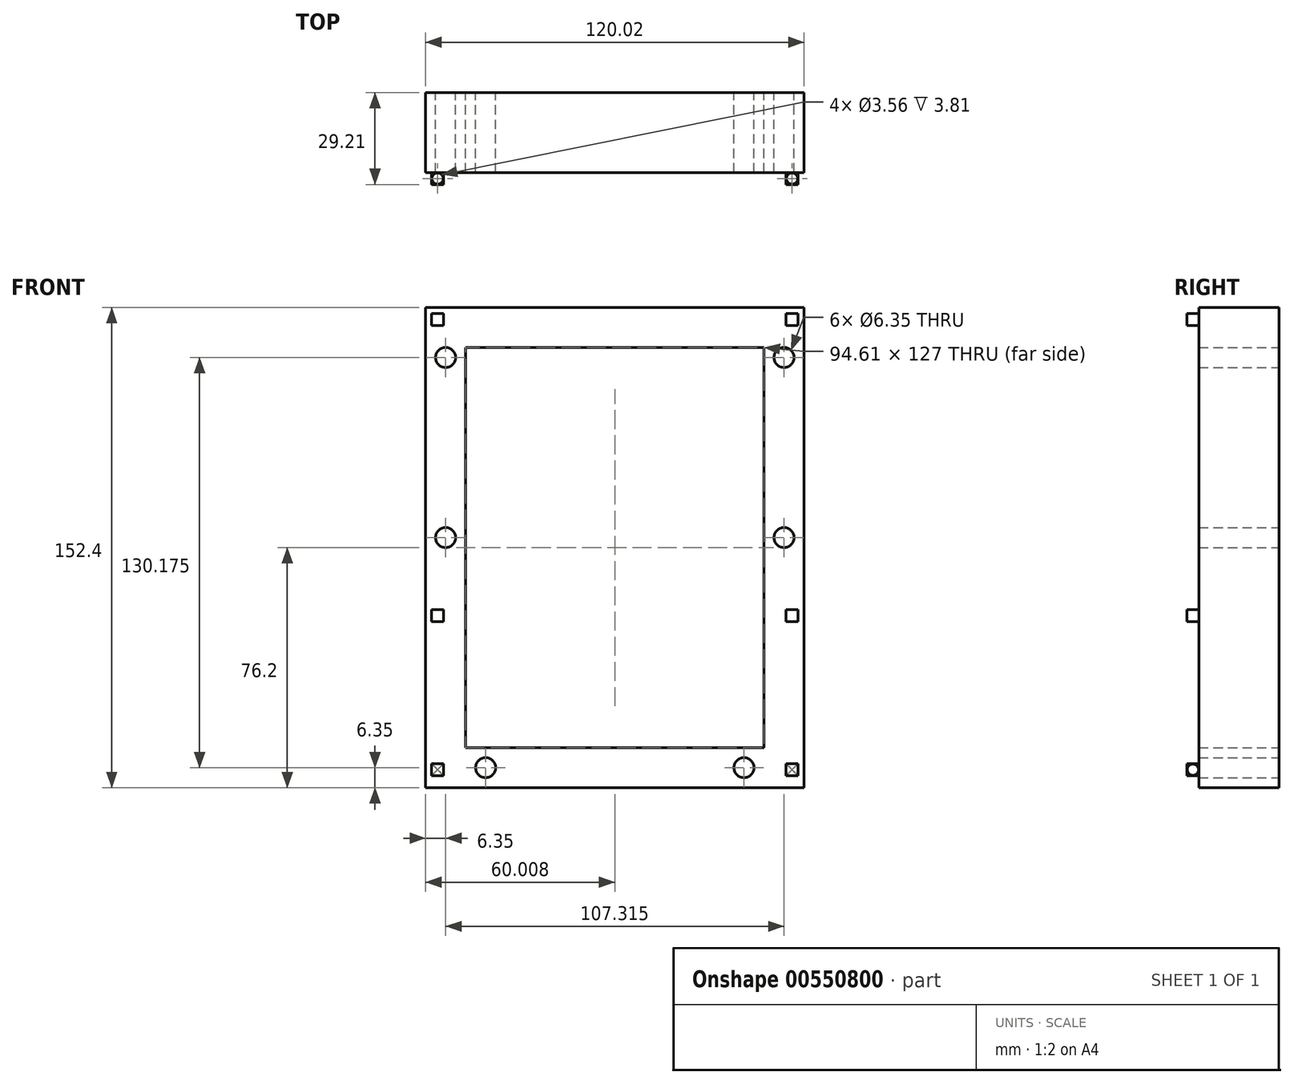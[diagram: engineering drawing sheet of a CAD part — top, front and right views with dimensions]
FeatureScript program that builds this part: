
annotation { "Feature Type Name" : "Feature", "Feature Type Description" : "" }
export const myFeature = defineFeature(function(context is Context, id is Id, definition is map)
    precondition{}
    {
        {
            var Q0;
            Q0=qCreatedBy(makeId("Front.planeOp"),FACE);
            var sketch = newSketch(context, id + "F0", { "sketchPlane" : qUnion([Q0])});
            skLineSegment(sketch, "E0.bottom", {"start": v(0, 0) * mm, "end": v(120.02, 0) * mm});
            skLineSegment(sketch, "E0.top", {"start": v(0, -152.4) * mm, "end": v(120.02, -152.4) * mm});
            skLineSegment(sketch, "E0.left", {"start": v(0, 0) * mm, "end": v(0, -152.4) * mm});
            skLineSegment(sketch, "E0.right", {"start": v(120.02, 0) * mm, "end": v(120.02, -152.4) * mm});
            skLineSegment(sketch, "E1", {"start": v(12.7, -12.7) * mm, "end": v(12.7, -139.7) * mm});
            skLineSegment(sketch, "E2", {"start": v(12.7, -12.7) * mm, "end": v(107.31, -12.7) * mm});
            skLineSegment(sketch, "E3", {"start": v(107.31, -12.7) * mm, "end": v(107.31, -139.7) * mm});
            skLineSegment(sketch, "E4", {"start": v(12.7, -139.7) * mm, "end": v(107.31, -139.7) * mm});
            skCircle(sketch, "E5", {"center": v(6.35, -15.88) * mm, "radius": 3.18 * mm});
            skCircle(sketch, "E6", {"center": v(6.35, -73.03) * mm, "radius": 3.18 * mm});
            skCircle(sketch, "E7", {"center": v(19.05, -146.05) * mm, "radius": 3.18 * mm});
            skLineSegment(sketch, "E8", {"start": v(60, 0) * mm, "end": v(60, -152.4) * mm, "construction": true});
            skCircle(sketch, "E9.MirrorC", {"center": v(113.66, -15.87) * mm, "radius": 3.18 * mm});
            skCircle(sketch, "E10.MirrorC", {"center": v(113.67, -73.03) * mm, "radius": 3.18 * mm});
            skCircle(sketch, "E11.MirrorC", {"center": v(100.97, -146.05) * mm, "radius": 3.18 * mm});
            skLineSegment(sketch, "E12", {"start": v(120.02, -101.6) * mm, "end": v(0, -101.6) * mm, "construction": true});
            skLineSegment(sketch, "E13", {"start": v(0, -7.62) * mm, "end": v(120.01, -7.62) * mm, "construction": true});
            skLineSegment(sketch, "E14", {"start": v(0, -93.98) * mm, "end": v(120.01, -93.98) * mm, "construction": true});
            skLineSegment(sketch, "E15", {"start": v(7.62, -101.6) * mm, "end": v(7.62, -152.4) * mm, "construction": true});
            skLineSegment(sketch, "E16", {"start": v(112.4, -101.6) * mm, "end": v(112.4, -152.4) * mm, "construction": true});
            skLineSegment(sketch, "E17.bottom", {"start": v(1.9, -144.78) * mm, "end": v(5.72, -144.78) * mm});
            skLineSegment(sketch, "E17.top", {"start": v(1.9, -148.6) * mm, "end": v(5.72, -148.6) * mm});
            skLineSegment(sketch, "E17.left", {"start": v(1.9, -144.78) * mm, "end": v(1.9, -148.59) * mm});
            skLineSegment(sketch, "E17.right", {"start": v(5.72, -144.78) * mm, "end": v(5.72, -148.59) * mm});
            skLineSegment(sketch, "E18.MirrorCS", {"start": v(118.11, -148.6) * mm, "end": v(114.3, -148.6) * mm});
            skLineSegment(sketch, "E19.MirrorCS", {"start": v(118.11, -144.78) * mm, "end": v(118.11, -148.59) * mm});
            skLineSegment(sketch, "E20.MirrorCS", {"start": v(118.11, -144.78) * mm, "end": v(114.3, -144.78) * mm});
            skLineSegment(sketch, "E21.MirrorCS", {"start": v(114.3, -144.78) * mm, "end": v(114.3, -148.59) * mm});
            skLineSegment(sketch, "E22.top", {"start": v(1.9, -101.6) * mm, "end": v(7.62, -101.6) * mm});
            skLineSegment(sketch, "E23", {"start": v(7.62, -101.6) * mm, "end": v(7.62, 0) * mm, "construction": true});
            skLineSegment(sketch, "E24.bottom", {"start": v(1.9, -95.88) * mm, "end": v(5.72, -95.88) * mm});
            skLineSegment(sketch, "E24.top", {"start": v(1.9, -99.7) * mm, "end": v(5.72, -99.7) * mm});
            skLineSegment(sketch, "E24.left", {"start": v(1.9, -95.88) * mm, "end": v(1.9, -99.7) * mm});
            skLineSegment(sketch, "E24.right", {"start": v(5.72, -95.88) * mm, "end": v(5.72, -99.7) * mm});
            skLineSegment(sketch, "E25.MirrorCS", {"start": v(118.11, -99.7) * mm, "end": v(114.3, -99.7) * mm});
            skLineSegment(sketch, "E26.MirrorCS", {"start": v(118.11, -95.88) * mm, "end": v(118.11, -99.7) * mm});
            skLineSegment(sketch, "E27.MirrorCS", {"start": v(118.11, -95.88) * mm, "end": v(114.3, -95.88) * mm});
            skLineSegment(sketch, "E28.MirrorCS", {"start": v(114.3, -95.88) * mm, "end": v(114.3, -99.7) * mm});
            skLineSegment(sketch, "E29.bottom", {"start": v(1.9, -1.9) * mm, "end": v(5.71, -1.9) * mm});
            skLineSegment(sketch, "E29.top", {"start": v(1.9, -5.71) * mm, "end": v(5.71, -5.71) * mm});
            skLineSegment(sketch, "E29.left", {"start": v(1.9, -1.9) * mm, "end": v(1.9, -5.71) * mm});
            skLineSegment(sketch, "E29.right", {"start": v(5.71, -1.9) * mm, "end": v(5.71, -5.71) * mm});
            skLineSegment(sketch, "E30.MirrorCS", {"start": v(118.11, -5.71) * mm, "end": v(114.3, -5.71) * mm});
            skLineSegment(sketch, "E31.MirrorCS", {"start": v(118.11, -1.9) * mm, "end": v(118.11, -5.71) * mm});
            skLineSegment(sketch, "E32.MirrorCS", {"start": v(118.11, -1.9) * mm, "end": v(114.3, -1.9) * mm});
            skLineSegment(sketch, "E33.MirrorCS", {"start": v(114.3, -1.9) * mm, "end": v(114.3, -5.72) * mm});
            skSolve(sketch);
        }
        {
            var Q0;
            Q0=makeQuery(id+"F0.imprint","IMPRINT",FACE,{"disambiguationData":[TD([[makeQuery(id+"F0.imprint","IMPRINT",EDGE,{"derivedFrom":sQuery(id+"F0.wireOp",EDGE,"E0.bottom")}),-1.0]])]});
            extrude(context, id + "F1", {"entities" : qUnion([Q0]), "depth" : 25.4 * mm, "offsetDistance" : 25.4 * mm});
        }
        {
            var Q0;
            Q0=makeQuery(id+"F0.imprint","IMPRINT",FACE,{"disambiguationData":[TD([[makeQuery(id+"F0.imprint","IMPRINT",EDGE,{"derivedFrom":sQuery(id+"F0.wireOp",EDGE,"E18.MirrorCS")}),-1.0]])]});
            var Q1;
            Q1=makeQuery(id+"F0.imprint","IMPRINT",FACE,{"disambiguationData":[TD([[makeQuery(id+"F0.imprint","IMPRINT",EDGE,{"derivedFrom":sQuery(id+"F0.wireOp",EDGE,"E17.bottom")}),-1.0]])]});
            extrude(context, id + "F2", {"entities" : qUnion([Q0, Q1]), "operationType" : NewBodyOperationType.ADD, "depth" : 29.2 * mm, "offsetDistance" : 25.4 * mm});
        }
        {
            var Q0;
            Q0=makeQuery(id+"F2.opExtrude","SWEPT_FACE",FACE,{"disambiguationData":[OSD([sQuery(id+"F0.wireOp",EDGE,"E17.left")])]});
            var sketch = newSketch(context, id + "F3", { "sketchPlane" : qUnion([Q0])});
            skCircle(sketch, "E34", {"center": v(27.3, -146.68) * mm, "radius": 1.78 * mm});
            skSolve(sketch);
        }
        {
            var Q0;
            Q0=makeQuery(id+"F3.imprint","IMPRINT",FACE,{"disambiguationData":[TD([[makeQuery(id+"F3.imprint","IMPRINT",EDGE,{"derivedFrom":sQuery(id+"F3.wireOp",EDGE,"E34")}),1.0]])]});
            extrude(context, id + "F4", {"entities" : qUnion([Q0]), "operationType" : NewBodyOperationType.REMOVE, "endBound" : BoundingType.THROUGH_ALL, "oppositeDirection" : true, "depth" : 25.4 * mm, "offsetDistance" : 25.4 * mm});
        }
        {
            var Q0;
            Q0=makeQuery(id+"F0.imprint","IMPRINT",FACE,{"disambiguationData":[TD([[makeQuery(id+"F0.imprint","IMPRINT",EDGE,{"derivedFrom":sQuery(id+"F0.wireOp",EDGE,"E25.MirrorCS")}),-1.0]])]});
            var Q1;
            Q1=makeQuery(id+"F0.imprint","IMPRINT",FACE,{"disambiguationData":[TD([[makeQuery(id+"F0.imprint","IMPRINT",EDGE,{"derivedFrom":sQuery(id+"F0.wireOp",EDGE,"E30.MirrorCS")}),-1.0]])]});
            var Q2;
            Q2=makeQuery(id+"F0.imprint","IMPRINT",FACE,{"disambiguationData":[TD([[makeQuery(id+"F0.imprint","IMPRINT",EDGE,{"derivedFrom":sQuery(id+"F0.wireOp",EDGE,"E29.bottom")}),-1.0]])]});
            var Q3;
            Q3=makeQuery(id+"F0.imprint","IMPRINT",FACE,{"disambiguationData":[TD([[makeQuery(id+"F0.imprint","IMPRINT",EDGE,{"derivedFrom":sQuery(id+"F0.wireOp",EDGE,"E24.bottom")}),-1.0]])]});
            extrude(context, id + "F5", {"entities" : qUnion([Q0, Q1, Q2, Q3]), "operationType" : NewBodyOperationType.ADD, "depth" : 29.2 * mm, "offsetDistance" : 25.4 * mm});
        }
        {
            var Q0;
            Q0=makeQuery(id+"F5.opExtrude","SWEPT_FACE",FACE,{"disambiguationData":[OSD([sQuery(id+"F0.wireOp",EDGE,"E29.bottom")])]});
            var sketch = newSketch(context, id + "F6", { "sketchPlane" : qUnion([Q0])});
            skCircle(sketch, "E35", {"center": v(3.8, -27.3) * mm, "radius": 1.78 * mm});
            skPoint(sketch, "E35.centerSnap0", {"position": v(3.8, -25.4) * mm});
            skSolve(sketch);
        }
        {
            var Q0;
            Q0=makeQuery(id+"F6.imprint","IMPRINT",FACE,{"disambiguationData":[TD([[makeQuery(id+"F6.imprint","IMPRINT",EDGE,{"derivedFrom":sQuery(id+"F6.wireOp",EDGE,"E35")}),1.0]])]});
            extrude(context, id + "F7", {"entities" : qUnion([Q0]), "operationType" : NewBodyOperationType.REMOVE, "endBound" : BoundingType.THROUGH_ALL, "oppositeDirection" : true, "depth" : 25.4 * mm, "offsetDistance" : 25.4 * mm});
        }
        {
            var Q0;
            Q0=makeQuery(id+"F5.opExtrude","SWEPT_FACE",FACE,{"disambiguationData":[OSD([sQuery(id+"F0.wireOp",EDGE,"E32.MirrorCS")])]});
            var sketch = newSketch(context, id + "F8", { "sketchPlane" : qUnion([Q0])});
            skCircle(sketch, "E36", {"center": v(116.2, -27.3) * mm, "radius": 1.78 * mm});
            skPoint(sketch, "E36.centerSnap0", {"position": v(116.2, -25.4) * mm});
            skSolve(sketch);
        }
        {
            var Q0;
            Q0=makeQuery(id+"F8.imprint","IMPRINT",FACE,{"disambiguationData":[TD([[makeQuery(id+"F8.imprint","IMPRINT",EDGE,{"derivedFrom":sQuery(id+"F8.wireOp",EDGE,"E36")}),1.0]])]});
            extrude(context, id + "F9", {"entities" : qUnion([Q0]), "operationType" : NewBodyOperationType.REMOVE, "endBound" : BoundingType.THROUGH_ALL, "oppositeDirection" : true, "depth" : 25.4 * mm, "offsetDistance" : 25.4 * mm});
        }
    });
